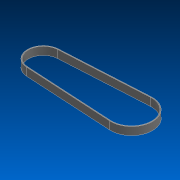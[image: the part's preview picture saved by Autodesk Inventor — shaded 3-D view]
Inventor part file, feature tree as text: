
AUTODESK INVENTOR PART (.ipt)
format: ipt  version: 2022.2 (Build 262287000, 287)  size: 97,792 bytes
history: native  units: in
note: dims shown in document units (in); Inventor stores cm internally (conversion verified against a paired STEP export)
features: extrude x1, sketch x1
ambient origin geometry x8: Origin, YZ Plane, XZ Plane, XY Plane, X Axis, Y Axis, Z Axis, Center Point
bodies: Solid1 (feature_tree)
feature tree (2):
  extrude  "Extrusion1"  Depth=0.0394in
  sketch  "Sketch1"  dims[d0=3.9805in d1=1.353in d2=1.805in d4=0.3543in d5=0.0in d6=0.0394in]
